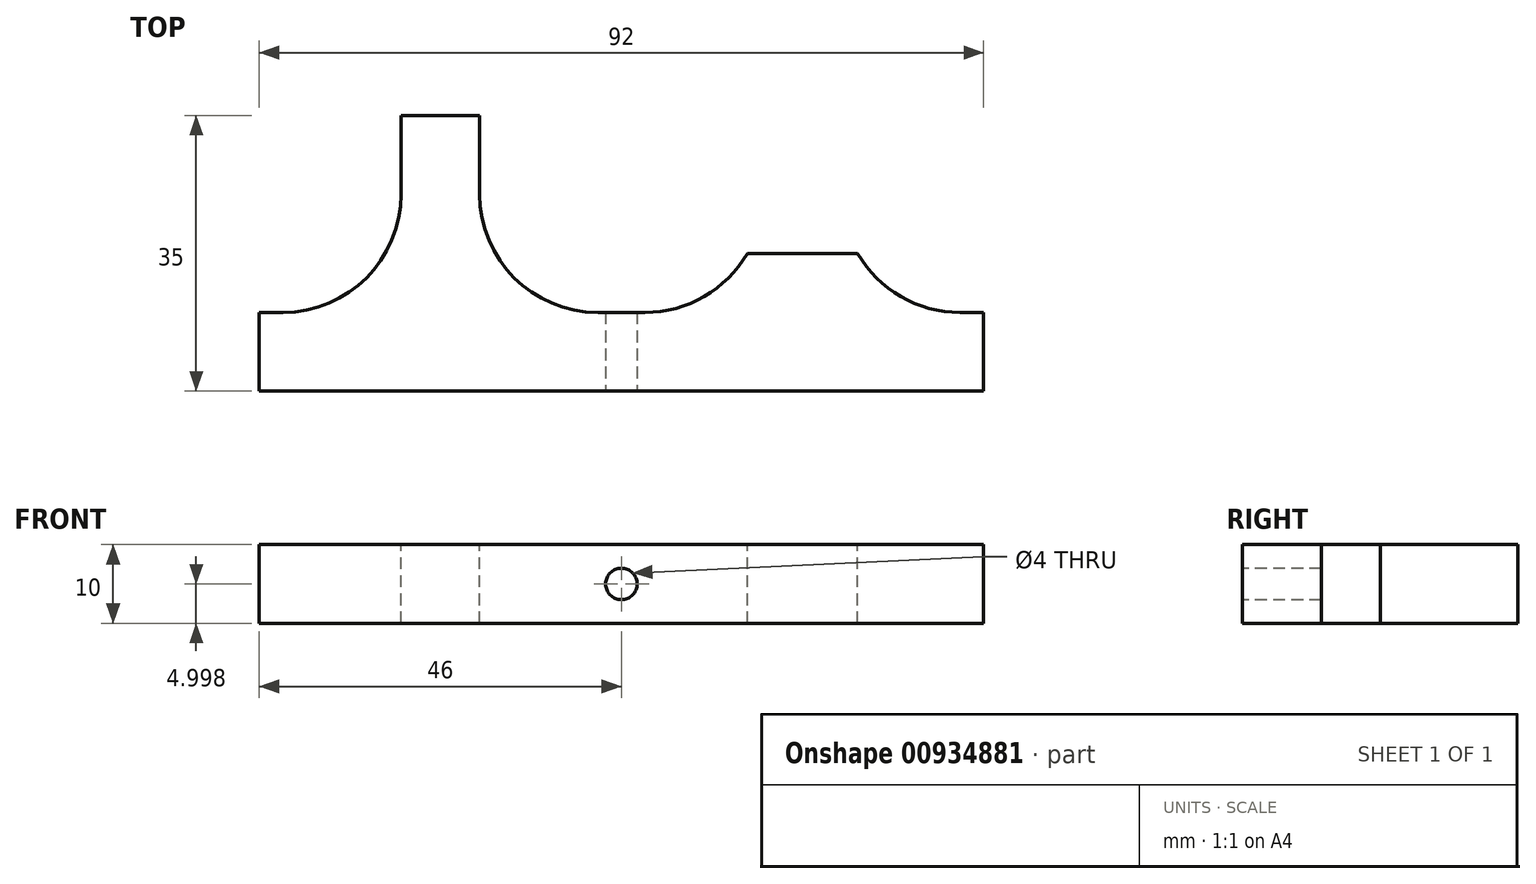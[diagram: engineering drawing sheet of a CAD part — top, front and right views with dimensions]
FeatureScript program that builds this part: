
annotation { "Feature Type Name" : "Feature", "Feature Type Description" : "" }
export const myFeature = defineFeature(function(context is Context, id is Id, definition is map)
    precondition{}
    {
        {
            var Q0;
            Q0=qCreatedBy(makeId("Front.planeOp"),FACE);
            var sketch = newSketch(context, id + "F0", { "sketchPlane" : qUnion([Q0])});
            skLineSegment(sketch, "E0.bottom", {"start": v(-28.16, 31.96) * mm, "end": v(63.84, 31.96) * mm});
            skLineSegment(sketch, "E0.top", {"start": v(-28.16, 21.96) * mm, "end": v(63.84, 21.96) * mm});
            skLineSegment(sketch, "E0.left", {"start": v(-28.16, 31.96) * mm, "end": v(-28.16, 21.96) * mm});
            skLineSegment(sketch, "E0.right", {"start": v(63.84, 31.96) * mm, "end": v(63.84, 21.96) * mm});
            skSolve(sketch);
        }
        {
            var Q0;
            Q0 = qSketchRegion(id + "F0", true);
            extrude(context, id + "F1", {"entities" : qUnion([Q0]), "depth" : 35 * mm, "offsetDistance" : 25 * mm});
        }
        {
            var Q0;
            Q0=makeQuery(id+"F1.opExtrude","SWEPT_FACE",FACE,{"disambiguationData":[OSD([sQuery(id+"F0.wireOp",EDGE,"E0.bottom")])]});
            var sketch = newSketch(context, id + "F2", { "sketchPlane" : qUnion([Q0])});
            skLineSegment(sketch, "E1.bottom", {"start": v(-0.16, 0) * mm, "end": v(35.84, 0) * mm});
            skLineSegment(sketch, "E1.top", {"start": v(-0.16, -25) * mm, "end": v(35.84, -25) * mm});
            skLineSegment(sketch, "E1.left", {"start": v(-0.16, 0) * mm, "end": v(-0.16, -25) * mm});
            skLineSegment(sketch, "E1.right", {"start": v(35.84, 0) * mm, "end": v(35.84, -25) * mm});
            skLineSegment(sketch, "E2.bottom", {"start": v(-28.16, 0) * mm, "end": v(-10.16, 0) * mm});
            skLineSegment(sketch, "E2.top", {"start": v(-28.16, -25) * mm, "end": v(-10.16, -25) * mm});
            skLineSegment(sketch, "E2.left", {"start": v(-28.16, 0) * mm, "end": v(-28.16, -25) * mm});
            skLineSegment(sketch, "E2.right", {"start": v(-10.16, 0) * mm, "end": v(-10.16, -25) * mm});
            skLineSegment(sketch, "E3.bottom", {"start": v(63.84, 0) * mm, "end": v(45.84, 0) * mm});
            skLineSegment(sketch, "E3.top", {"start": v(63.84, -25) * mm, "end": v(45.84, -25) * mm});
            skLineSegment(sketch, "E3.left", {"start": v(63.84, 0) * mm, "end": v(63.84, -25) * mm});
            skLineSegment(sketch, "E3.right", {"start": v(45.84, 0) * mm, "end": v(45.84, -25) * mm});
            skSolve(sketch);
        }
        {
            var Q0;
            Q0=makeQuery(id+"F2.imprint","IMPRINT",FACE,{"disambiguationData":[TD([[makeQuery(id+"F2.imprint","IMPRINT",EDGE,{"derivedFrom":sQuery(id+"F2.wireOp",EDGE,"E2.bottom")}),-1.0]])]});
            var Q1;
            Q1=makeQuery(id+"F2.imprint","IMPRINT",FACE,{"disambiguationData":[TD([[makeQuery(id+"F2.imprint","IMPRINT",EDGE,{"derivedFrom":sQuery(id+"F2.wireOp",EDGE,"E1.bottom")}),-1.0]])]});
            var Q2;
            Q2=makeQuery(id+"F2.imprint","IMPRINT",FACE,{"disambiguationData":[TD([[makeQuery(id+"F2.imprint","IMPRINT",EDGE,{"derivedFrom":sQuery(id+"F2.wireOp",EDGE,"E3.bottom")}),-1.0]])]});
            extrude(context, id + "F3", {"entities" : qUnion([Q0, Q1, Q2]), "operationType" : NewBodyOperationType.REMOVE, "oppositeDirection" : true, "depth" : 10 * mm, "offsetDistance" : 25 * mm});
        }
        {
            var Q0;
            Q0=makeQuery(id+"F1.opExtrude","CAP_FACE",FACE,{"disambiguationData":[OSD([sQuery(id+"F0.wireOp",EDGE,"E0.bottom"),sQuery(id+"F0.wireOp",EDGE,"E0.top"),sQuery(id+"F0.wireOp",EDGE,"E0.left"),sQuery(id+"F0.wireOp",EDGE,"E0.right")])],"isStart":false});
            var sketch = newSketch(context, id + "F4", { "sketchPlane" : qUnion([Q0])});
            skCircle(sketch, "E4", {"center": v(17.84, 26.96) * mm, "radius": 2 * mm});
            skSolve(sketch);
        }
        {
            var Q0;
            Q0=makeQuery(id+"F4.imprint","IMPRINT",FACE,{"disambiguationData":[TD([[makeQuery(id+"F4.imprint","IMPRINT",EDGE,{"derivedFrom":sQuery(id+"F4.wireOp",EDGE,"E4")}),1.0]])]});
            extrude(context, id + "F5", {"entities" : qUnion([Q0]), "operationType" : NewBodyOperationType.REMOVE, "oppositeDirection" : true, "depth" : 10 * mm, "offsetDistance" : 25 * mm});
        }
        {
            var Q0;
            Q0=makeQuery(id+"F3.boolean.opBoolean","COPY",EDGE,{"derivedFrom":makeQuery(id+"F3.opExtrude","SWEPT_EDGE",EDGE,{"disambiguationData":[OSD([sQuery(id+"F2.wireOp",EDGE,"E1.top"),sQuery(id+"F2.wireOp",EDGE,"E1.left")])]})});
            var Q1;
            Q1=makeQuery(id+"F3.boolean.opBoolean","COPY",EDGE,{"derivedFrom":makeQuery(id+"F3.opExtrude","SWEPT_EDGE",EDGE,{"disambiguationData":[OSD([sQuery(id+"F2.wireOp",EDGE,"E3.top"),sQuery(id+"F2.wireOp",EDGE,"E3.right")])]})});
            var Q2;
            Q2=makeQuery(id+"F3.boolean.opBoolean","COPY",EDGE,{"derivedFrom":makeQuery(id+"F3.opExtrude","SWEPT_EDGE",EDGE,{"disambiguationData":[OSD([sQuery(id+"F2.wireOp",EDGE,"E1.top"),sQuery(id+"F2.wireOp",EDGE,"E1.right")])]})});
            var Q3;
            Q3=makeQuery(id+"F3.boolean.opBoolean","COPY",EDGE,{"derivedFrom":makeQuery(id+"F3.opExtrude","SWEPT_EDGE",EDGE,{"disambiguationData":[OSD([sQuery(id+"F2.wireOp",EDGE,"E2.top"),sQuery(id+"F2.wireOp",EDGE,"E2.right")])]})});
            fillet(context, id + "F6", {"entities" : qUnion([Q0, Q1, Q2, Q3]), "radius" : 15 * mm, "tangentPropagation" : true, "allowEdgeOverflow" : false});
        }
        {
            var Q0;
            {var subQ0=sQuery(id+"F0.wireOp",EDGE,"E0.bottom");var subQ1=sQuery(id+"F0.wireOp",EDGE,"E0.top");Q0=makeQuery(id+"F3.boolean.opBoolean","SPLIT",FACE,{"disambiguationData":[TD([makeQuery(id+"F3.opExtrude","SWEPT_FACE",FACE,{"disambiguationData":[OSD([sQuery(id+"F2.wireOp",EDGE,"E1.right")])]})])],"derivedFrom":makeQuery(id+"F1.opExtrude","CAP_FACE",FACE,{"disambiguationData":[OSD([subQ0,subQ1,sQuery(id+"F0.wireOp",EDGE,"E0.left"),sQuery(id+"F0.wireOp",EDGE,"E0.right")])],"isStart":true})});}
            var sketch = newSketch(context, id + "F7", { "sketchPlane" : qUnion([Q0])});
            skLineSegment(sketch, "E5.bottom", {"start": v(-35.84, 21.96) * mm, "end": v(-45.84, 21.96) * mm});
            skLineSegment(sketch, "E5.top", {"start": v(-35.84, 31.96) * mm, "end": v(-45.84, 31.96) * mm});
            skLineSegment(sketch, "E5.left", {"start": v(-35.84, 21.96) * mm, "end": v(-35.84, 31.96) * mm});
            skLineSegment(sketch, "E5.right", {"start": v(-45.84, 21.96) * mm, "end": v(-45.84, 31.96) * mm});
            skLineSegment(sketch, "E6.bottom", {"start": v(-30.94, 21.96) * mm, "end": v(-50.94, 21.96) * mm});
            skLineSegment(sketch, "E6.top", {"start": v(-30.94, 31.96) * mm, "end": v(-50.94, 31.96) * mm});
            skLineSegment(sketch, "E6.left", {"start": v(-30.94, 21.96) * mm, "end": v(-30.94, 31.96) * mm});
            skLineSegment(sketch, "E6.right", {"start": v(-50.94, 21.96) * mm, "end": v(-50.94, 31.96) * mm});
            skSolve(sketch);
        }
        {
            var Q0;
            Q0 = qSketchRegion(id + "F7", true);
            extrude(context, id + "F8", {"entities" : qUnion([Q0]), "operationType" : NewBodyOperationType.REMOVE, "oppositeDirection" : true, "depth" : 17.5 * mm, "offsetDistance" : 25 * mm});
        }
    });
